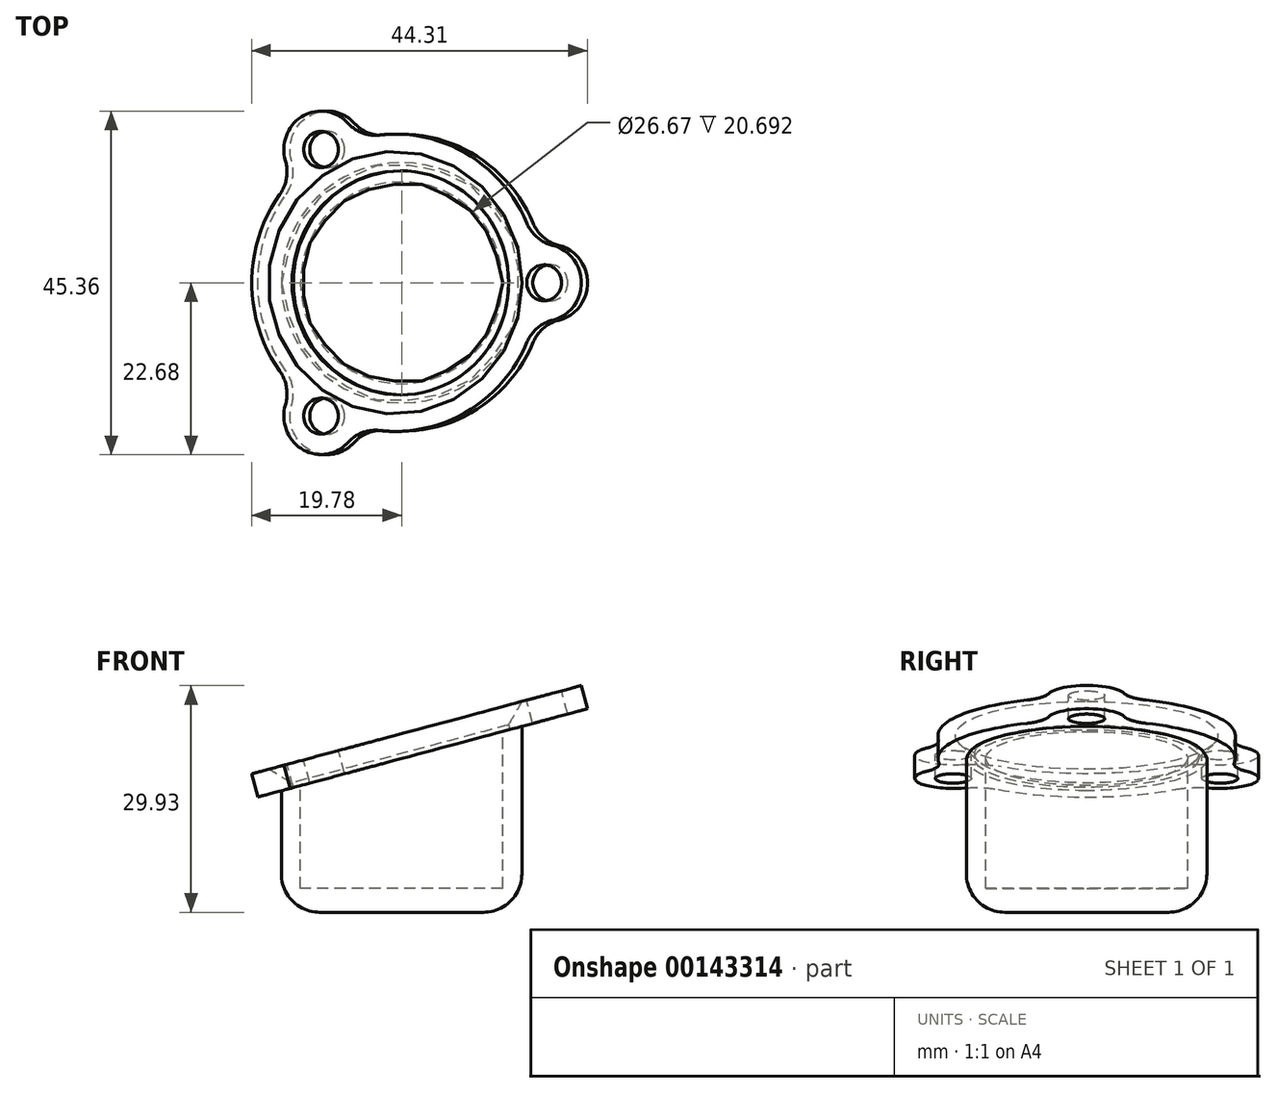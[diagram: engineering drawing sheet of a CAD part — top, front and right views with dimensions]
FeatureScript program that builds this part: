
annotation { "Feature Type Name" : "Feature", "Feature Type Description" : "" }
export const myFeature = defineFeature(function(context is Context, id is Id, definition is map)
    precondition{}
    {
        {
            var Q0;
            Q0=qCreatedBy(makeId("Top.planeOp"),FACE);
            var sketch = newSketch(context, id + "F0", { "sketchPlane" : qUnion([Q0])});
            skCircle(sketch, "E0", {"center": v(0, 0) * mm, "radius": 15.88 * mm});
            skSolve(sketch);
        }
        {
            var Q0;
            Q0 = qSketchRegion(id + "F0", true);
            extrude(context, id + "F1", {"entities" : qUnion([Q0]), "depth" : 25.4 * mm, "offsetDistance" : 25.4 * mm});
        }
        {
            var Q0;
            Q0=makeQuery(id+"F1.opExtrude","CAP_FACE",FACE,{"disambiguationData":[OSD([sQuery(id+"F0.wireOp",EDGE,"E0")])],"isStart":false});
            var sketch = newSketch(context, id + "F2", { "sketchPlane" : qUnion([Q0])});
            skCircle(sketch, "E1", {"center": v(0, 0) * mm, "radius": 13.34 * mm});
            skSolve(sketch);
        }
        {
            var Q0;
            Q0 = qSketchRegion(id + "F2", true);
            extrude(context, id + "F3", {"entities" : qUnion([Q0]), "operationType" : NewBodyOperationType.REMOVE, "oppositeDirection" : true, "depth" : 22.22 * mm, "offsetDistance" : 25.4 * mm});
        }
        {
            var Q0;
            Q0=qCreatedBy(makeId("Front.planeOp"),FACE);
            var sketch = newSketch(context, id + "F4", { "sketchPlane" : qUnion([Q0])});
            skLineSegment(sketch, "E2", {"start": v(-16.82, 25.4) * mm, "end": v(19.06, 25.4) * mm});
            skLineSegment(sketch, "E3", {"start": v(19.06, 25.4) * mm, "end": v(-16.82, 15.79) * mm});
            skLineSegment(sketch, "E4", {"start": v(-16.82, 15.79) * mm, "end": v(-16.82, 25.4) * mm});
            skSolve(sketch);
        }
        {
            var Q0;
            Q0=makeQuery(id+"F4.imprint","IMPRINT",FACE,{"disambiguationData":[TD([[makeQuery(id+"F4.imprint","IMPRINT",EDGE,{"derivedFrom":sQuery(id+"F4.wireOp",EDGE,"E2")}),-1.0]])]});
            extrude(context, id + "F5", {"entities" : qUnion([Q0]), "operationType" : NewBodyOperationType.REMOVE, "oppositeDirection" : true, "depth" : 127 * mm, "offsetDistance" : 25.4 * mm, "symmetric" : true});
        }
        {
            var Q0;
            Q0=makeQuery(id+"F5.boolean.opBoolean","COPY",FACE,{"derivedFrom":makeQuery(id+"F5.opExtrude","SWEPT_FACE",FACE,{"disambiguationData":[OSD([sQuery(id+"F4.wireOp",EDGE,"E3")])]})});
            var sketch = newSketch(context, id + "F6", { "sketchPlane" : qUnion([Q0])});
            skCircle(sketch, "E5", {"center": v(5.25, 0) * mm, "radius": 14.8 * mm});
            skCircle(sketch, "E6", {"center": v(5.25, 0) * mm, "radius": 25.4 * mm});
            skSolve(sketch);
        }
        {
            var Q0;
            Q0 = qSketchRegion(id + "F6", true);
            extrude(context, id + "F7", {"entities" : qUnion([Q0]), "operationType" : NewBodyOperationType.ADD, "depth" : 3.17 * mm, "offsetDistance" : 25.4 * mm});
        }
        {
            var Q0;
            Q0=makeQuery(id+"F7.opExtrude","CAP_FACE",FACE,{"disambiguationData":[OSD([sQuery(id+"F6.wireOp",EDGE,"E5"),sQuery(id+"F6.wireOp",EDGE,"E6")])],"isStart":false});
            var sketch = newSketch(context, id + "F8", { "sketchPlane" : qUnion([Q0])});
            skLineSegment(sketch, "E7", {"start": v(5.25, 0) * mm, "end": v(25.57, 0) * mm});
            skCircle(sketch, "E8", {"center": v(25.57, 0) * mm, "radius": 2.38 * mm});
            skCircle(sketch, "E9.1.0", {"center": v(-4.9, 17.6) * mm, "radius": 2.38 * mm});
            skCircle(sketch, "E9.2.0", {"center": v(-4.9, -17.6) * mm, "radius": 2.38 * mm});
            skPoint(sketch, "E9.center", {"position": v(5.25, 0) * mm});
            skSolve(sketch);
        }
        {
            var Q0;
            Q0 = qSketchRegion(id + "F8", true);
            extrude(context, id + "F9", {"entities" : qUnion([Q0]), "operationType" : NewBodyOperationType.REMOVE, "oppositeDirection" : true, "depth" : 25.4 * mm, "offsetDistance" : 25.4 * mm});
        }
        {
            var Q0;
            Q0=makeQuery(id+"F1.opExtrude","CAP_EDGE",EDGE,{"disambiguationData":[OSD([sQuery(id+"F0.wireOp",EDGE,"E0")])],"isStart":true});
            fillet(context, id + "F10", {"entities" : qUnion([Q0]), "radius" : 5.08 * mm, "tangentPropagation" : true, "allowEdgeOverflow" : false});
        }
        {
            var Q0;
            Q0=makeQuery(id+"F7.opExtrude","CAP_FACE",FACE,{"disambiguationData":[OSD([sQuery(id+"F6.wireOp",EDGE,"E5"),sQuery(id+"F6.wireOp",EDGE,"E6")])],"isStart":true});
            var sketch = newSketch(context, id + "F11", { "sketchPlane" : qUnion([Q0])});
            skCircle(sketch, "E10", {"center": v(-4.9, -17.6) * mm, "radius": 5.08 * mm});
            skCircle(sketch, "E11", {"center": v(-4.9, 17.6) * mm, "radius": 5.08 * mm});
            skCircle(sketch, "E12", {"center": v(25.57, 0) * mm, "radius": 5.08 * mm});
            skArc(sketch, "E13", {"start": v(0, -18.9) * mm, "mid": v(15.06, -17) * mm, "end": v(24.25, -4.9) * mm});
            skArc(sketch, "E14.1.0", {"start": v(24.25, 4.9) * mm, "mid": v(15.06, 17) * mm, "end": v(0, 18.9) * mm});
            skArc(sketch, "E14.2.0", {"start": v(-8.5, 14) * mm, "mid": v(-14.37, 0) * mm, "end": v(-8.5, -14) * mm});
            skCircle(sketch, "E15", {"center": v(5.25, 0) * mm, "radius": 25.4 * mm});
            skSolve(sketch);
        }
        {
            var Q0;
            {var subQ0=sQuery(id+"F11.wireOp",EDGE,"E13");Q0=makeQuery(id+"F11.imprint","IMPRINT",FACE,{"disambiguationData":[TD([[makeQuery(id+"F11.imprint","IMPRINT",EDGE,{"derivedFrom":subQ0}),-1.0]])]});}
            var Q1;
            {var subQ0=sQuery(id+"F11.wireOp",EDGE,"E14.2.0");Q1=makeQuery(id+"F11.imprint","IMPRINT",FACE,{"disambiguationData":[TD([[makeQuery(id+"F11.imprint","IMPRINT",EDGE,{"derivedFrom":subQ0}),-1.0]])]});}
            var Q2;
            {var subQ0=sQuery(id+"F11.wireOp",EDGE,"E14.1.0");Q2=makeQuery(id+"F11.imprint","IMPRINT",FACE,{"disambiguationData":[TD([[makeQuery(id+"F11.imprint","IMPRINT",EDGE,{"derivedFrom":subQ0}),-1.0]])]});}
            extrude(context, id + "F12", {"entities" : qUnion([Q0, Q1, Q2]), "operationType" : NewBodyOperationType.REMOVE, "endBound" : BoundingType.THROUGH_ALL, "oppositeDirection" : true, "depth" : 25.4 * mm, "offsetDistance" : 25.4 * mm});
        }
        {
            var Q0;
            Q0=makeQuery(id+"F7.opExtrude","CAP_EDGE",EDGE,{"disambiguationData":[OSD([sQuery(id+"F6.wireOp",EDGE,"E5")])],"isStart":false});
            chamfer(context, id + "F13", {"entities" : qUnion([Q0]), "width" : 2.54 * mm, "tangentPropagation" : true});
        }
        {
            var Q0;
            Q0=makeQuery(id+"F12.boolean.opBoolean","COPY",EDGE,{"derivedFrom":makeQuery(id+"F12.opExtrude","SWEPT_EDGE",EDGE,{"disambiguationData":[OSD([sQuery(id+"F11.wireOp",EDGE,"E11"),sQuery(id+"F11.wireOp",EDGE,"E14.1.0")])]})});
            var Q1;
            Q1=makeQuery(id+"F12.boolean.opBoolean","COPY",EDGE,{"derivedFrom":makeQuery(id+"F12.opExtrude","SWEPT_EDGE",EDGE,{"disambiguationData":[OSD([sQuery(id+"F11.wireOp",EDGE,"E11"),sQuery(id+"F11.wireOp",EDGE,"E14.2.0")])]})});
            var Q2;
            Q2=makeQuery(id+"F12.boolean.opBoolean","COPY",EDGE,{"derivedFrom":makeQuery(id+"F12.opExtrude","SWEPT_EDGE",EDGE,{"disambiguationData":[OSD([sQuery(id+"F11.wireOp",EDGE,"E10"),sQuery(id+"F11.wireOp",EDGE,"E14.2.0")])]})});
            var Q3;
            Q3=makeQuery(id+"F12.boolean.opBoolean","COPY",EDGE,{"derivedFrom":makeQuery(id+"F12.opExtrude","SWEPT_EDGE",EDGE,{"disambiguationData":[OSD([sQuery(id+"F11.wireOp",EDGE,"E10"),sQuery(id+"F11.wireOp",EDGE,"E13")])]})});
            var Q4;
            Q4=makeQuery(id+"F12.boolean.opBoolean","COPY",EDGE,{"derivedFrom":makeQuery(id+"F12.opExtrude","SWEPT_EDGE",EDGE,{"disambiguationData":[OSD([sQuery(id+"F11.wireOp",EDGE,"E12"),sQuery(id+"F11.wireOp",EDGE,"E13")])]})});
            var Q5;
            Q5=makeQuery(id+"F12.boolean.opBoolean","COPY",EDGE,{"derivedFrom":makeQuery(id+"F12.opExtrude","SWEPT_EDGE",EDGE,{"disambiguationData":[OSD([sQuery(id+"F11.wireOp",EDGE,"E12"),sQuery(id+"F11.wireOp",EDGE,"E14.1.0")])]})});
            fillet(context, id + "F14", {"entities" : qUnion([Q0, Q1, Q2, Q3, Q4, Q5]), "radius" : 5.08 * mm, "tangentPropagation" : true, "allowEdgeOverflow" : false});
        }
    });
